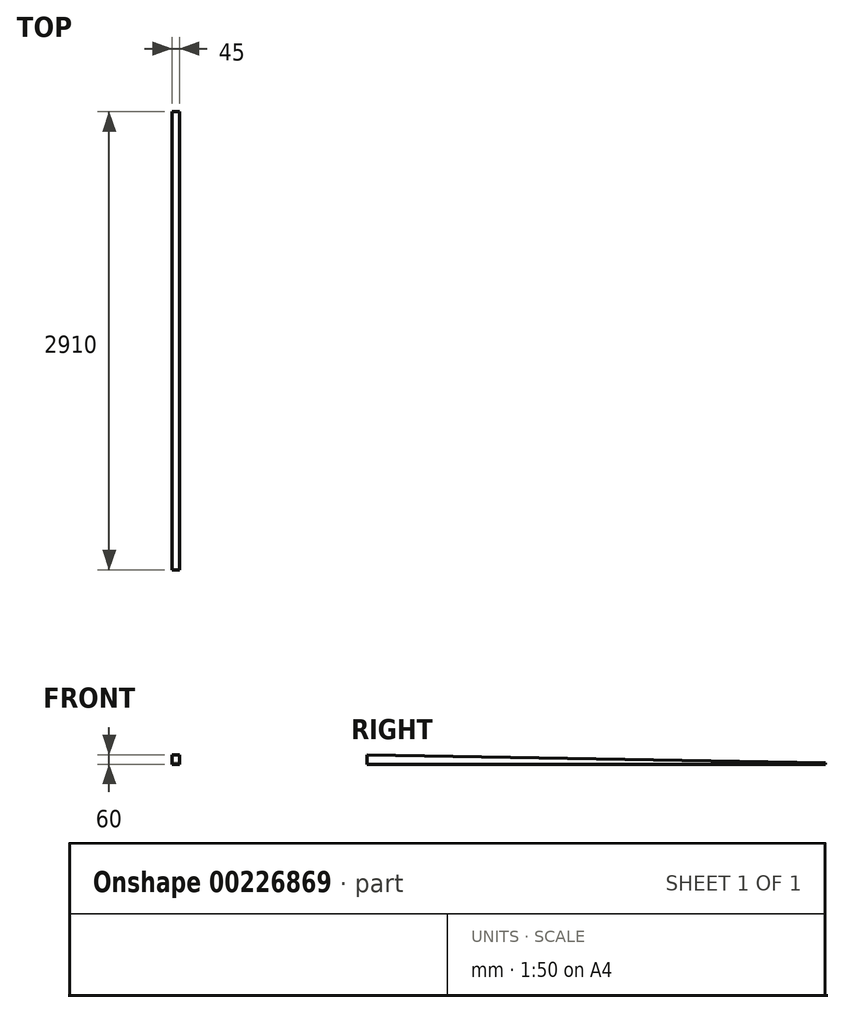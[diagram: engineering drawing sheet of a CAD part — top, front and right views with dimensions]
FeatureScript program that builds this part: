
annotation { "Feature Type Name" : "Feature", "Feature Type Description" : "" }
export const myFeature = defineFeature(function(context is Context, id is Id, definition is map)
    precondition{}
    {
        {
            var Q0;
            Q0=qCreatedBy(makeId("Right.planeOp"),FACE);
            var sketch = newSketch(context, id + "F0", { "sketchPlane" : qUnion([Q0])});
            skLineSegment(sketch, "E0", {"start": v(0, 0) * mm, "end": v(2910, 0) * mm});
            skLineSegment(sketch, "E1", {"start": v(2910, 10) * mm, "end": v(0, 60) * mm});
            skLineSegment(sketch, "E2", {"start": v(0, 60) * mm, "end": v(0, 0) * mm});
            skLineSegment(sketch, "E3", {"start": v(2910, 0) * mm, "end": v(2910, 10) * mm});
            skSolve(sketch);
        }
        {
            var Q0;
            Q0=makeQuery(id+"F0.imprint","IMPRINT",FACE,{"disambiguationData":[TD([[makeQuery(id+"F0.imprint","IMPRINT",EDGE,{"derivedFrom":sQuery(id+"F0.wireOp",EDGE,"E0")}),1.0]])]});
            extrude(context, id + "F1", {"entities" : qUnion([Q0]), "endBound" : BoundingType.SYMMETRIC, "depth" : 45 * mm});
        }
    });
